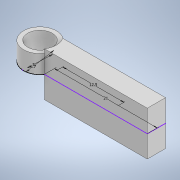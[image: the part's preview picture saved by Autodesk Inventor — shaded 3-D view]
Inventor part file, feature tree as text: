
AUTODESK INVENTOR PART (.ipt)
format: ipt  version: 2022 (Build 260153000, 153)  size: 108,544 bytes
history: native  units: in
note: dims shown in document units (in); Inventor stores cm internally (conversion verified against a paired STEP export)
features: extrude x2, sketch x1
ambient origin geometry x8: Origin, YZ Plane, XZ Plane, XY Plane, X Axis, Y Axis, Z Axis, Center Point
bodies: Solid1 (feature_tree)
feature tree (3):
  sketch  "Sketch1"  dims[d0=0.1969in d1=0.2638in d2=0.4921in d8=0.1457in d9=0.0in d12=0.8268in d13=0.3543in d14=0.0in]
  extrude  "Extrusion1"  Depth=0.3543in
  extrude  "Extrusion3"  Depth=0.3543in
